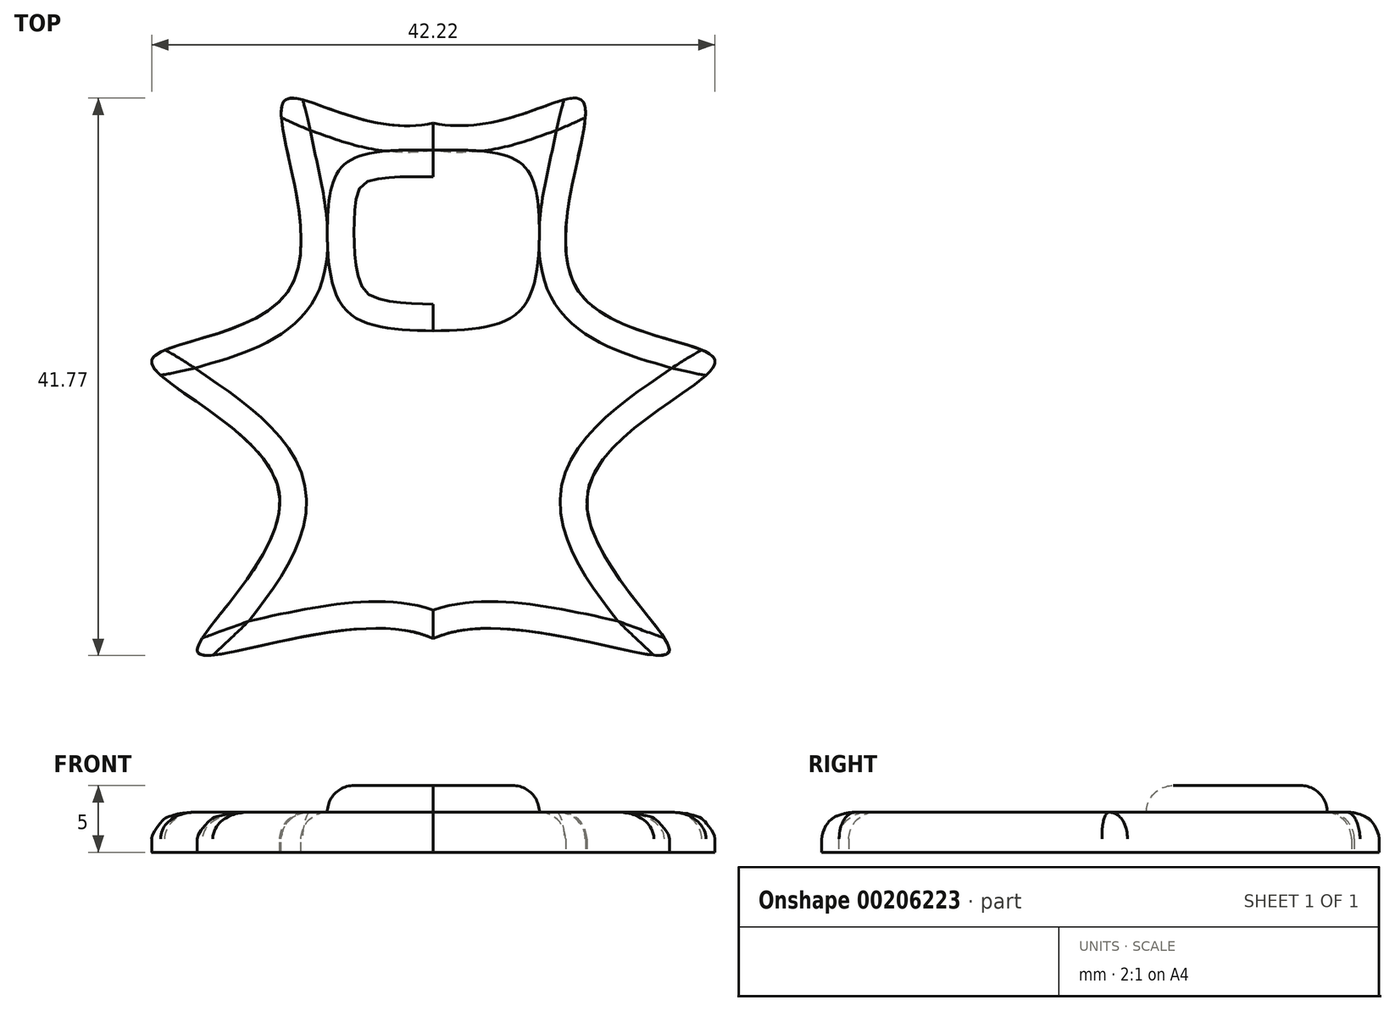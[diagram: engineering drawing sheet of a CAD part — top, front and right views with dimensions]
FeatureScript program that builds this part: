
annotation { "Feature Type Name" : "Feature", "Feature Type Description" : "" }
export const myFeature = defineFeature(function(context is Context, id is Id, definition is map)
    precondition{}
    {
        {
            var Q0;
            Q0=qCreatedBy(makeId("Top.planeOp"),FACE);
            var sketch = newSketch(context, id + "F0", { "sketchPlane" : qUnion([Q0])});
            skFitSpline(sketch, "E0", {"points": [v(0, 17.86) * mm, v(11.24, 19.43) * mm, v(10.79, 5.38) * mm, v(21.11, 0) * mm, v(11.54, -9.92) * mm, v(17.66, -21.8) * mm, v(0, -20.8) * mm], "startDerivative": vector(104.92, -22.79) * mm, "endDerivative": vector(-88.4, -41.3) * mm});
            skLineSegment(sketch, "E1", {"start": v(0, 17.86) * mm, "end": v(0, -20.8) * mm, "construction": true});
            skFitSpline(sketch, "E2.MirrorCS", {"points": [v(0, 17.86) * mm, v(-11.24, 19.43) * mm, v(-10.79, 5.38) * mm, v(-21.11, 0) * mm, v(-11.54, -9.92) * mm, v(-17.66, -21.8) * mm, v(0, -20.8) * mm], "startDerivative": vector(-104.92, -22.79) * mm, "endDerivative": vector(88.4, -41.3) * mm});
            skSolve(sketch);
        }
        {
            var Q0;
            Q0=makeQuery(id+"F0.imprint","IMPRINT",FACE,{"disambiguationData":[TD([[makeQuery(id+"F0.imprint","IMPRINT",EDGE,{"derivedFrom":sQuery(id+"F0.wireOp",EDGE,"E0")}),-1.0]])]});
            extrude(context, id + "F1", {"entities" : qUnion([Q0]), "depth" : 3 * mm});
        }
        {
            var Q0;
            Q0=makeQuery(id+"F1.opExtrude","CAP_EDGE",EDGE,{"disambiguationData":[OSD([sQuery(id+"F0.wireOp",EDGE,"E2.MirrorCS")])],"isStart":false});
            var Q1;
            Q1=makeQuery(id+"F1.opExtrude","CAP_EDGE",EDGE,{"disambiguationData":[OSD([sQuery(id+"F0.wireOp",EDGE,"E0")])],"isStart":false});
            fillet(context, id + "F2", {"entities" : qUnion([Q0, Q1]), "radius" : 2 * mm, "tangentPropagation" : true, "allowEdgeOverflow" : false});
        }
        {
            var Q0;
            Q0=makeQuery(id+"F1.opExtrude","CAP_FACE",FACE,{"disambiguationData":[OSD([sQuery(id+"F0.wireOp",EDGE,"E0"),sQuery(id+"F0.wireOp",EDGE,"E2.MirrorCS")])],"isStart":false});
            var sketch = newSketch(context, id + "F3", { "sketchPlane" : qUnion([Q0])});
            skFitSpline(sketch, "E3", {"points": [v(0, 15.82) * mm, v(-6.6, 14.8) * mm, v(-7.94, 10.03) * mm, v(-6.48, 3.78) * mm, v(0, 2.28) * mm], "startDerivative": vector(-30.4, 0.45) * mm, "endDerivative": vector(29.6, -0.77) * mm});
            skLineSegment(sketch, "E4", {"start": v(0, 15.82) * mm, "end": v(0, 2.28) * mm, "construction": true});
            skFitSpline(sketch, "E5.MirrorCS", {"points": [v(0, 15.82) * mm, v(6.6, 14.8) * mm, v(7.94, 10.03) * mm, v(6.48, 3.78) * mm, v(0, 2.28) * mm], "startDerivative": vector(30.4, 0.45) * mm, "endDerivative": vector(-29.6, -0.77) * mm});
            skSolve(sketch);
        }
        {
            var Q0;
            Q0 = qSketchRegion(id + "F3", true);
            extrude(context, id + "F4", {"entities" : qUnion([Q0]), "operationType" : NewBodyOperationType.ADD, "depth" : 2 * mm});
        }
        {
            var Q0;
            Q0=makeQuery(id+"F4.opExtrude","CAP_EDGE",EDGE,{"disambiguationData":[OSD([sQuery(id+"F3.wireOp",EDGE,"E3")])],"isStart":false});
            var Q1;
            Q1=makeQuery(id+"F4.opExtrude","CAP_EDGE",EDGE,{"disambiguationData":[OSD([sQuery(id+"F3.wireOp",EDGE,"E5.MirrorCS")])],"isStart":false});
            fillet(context, id + "F5", {"entities" : qUnion([Q0, Q1]), "radius" : 2 * mm, "tangentPropagation" : true, "allowEdgeOverflow" : false});
        }
    });
